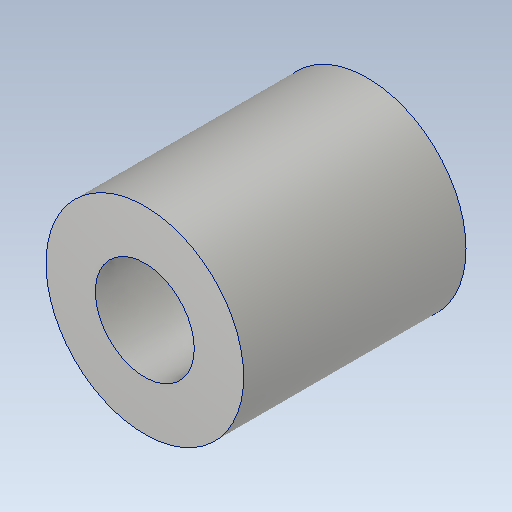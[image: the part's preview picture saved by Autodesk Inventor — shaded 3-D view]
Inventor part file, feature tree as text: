
AUTODESK INVENTOR PART (.ipt)
format: ipt  version: 2020.2 (Build 242310000, 310)  size: 114,176 bytes
history: native  units: mm
features: other x1, extrude x1, sketch x1
ambient origin geometry x8: Origin, YZ Plane, XZ Plane, XY Plane, X Axis, Y Axis, Z Axis, Center Point
bodies: Body1 (feature_tree)
feature tree (3):
  other  "ソリッド1"
  extrude  "押し出し1"  Depth=4.0mm
  sketch  "スケッチ1"
